# Revit family: Legrand Transformateur sec HP 2000kVA HN4AIAGPA
name_source: partatom
category: Equipement électrique
revit_build: Autodesk Revit 2018 (Build: 20170223_1515(x64)
units: mm (PartAtom-declared; Revit-internal decimal feet)

## family parameters
Basée sur le plan de construction = Non
Cote de connecteur circulaire = Utiliser le diamètre
Couper avec des vides une fois chargée = Non
Partagée = Non
Point de calcul de pièce = Non
Toujours verticalement = Oui
Type d'élément = Transformateur

## types (1)
- ZUHN4AIAGPA
    Classe d'isolement = 24 kV
    Conditions Générale d'Utilisation = https://export.legrand.com
    Coût = 0 $
    Description = Transformateur sec HP (Haute Performance) ZUHN4AIAGPA
    Enveloppe compatible IP31 = ZUBXS31CM
    Fabricant = Legrand
    Hauteur = 2420mm
    Ic - wheel centre line = 670
    Io = 0%
    Largeur = 2000mm
    LwA-Puissance acoustique = 71
    Pk at 120°C = 19000 W
    Po = 3100 W
    Poids = 6200Kg
    Puissance = 2000kVA
    R - wheel diameter = 160
    Tension = 20kV/410V
    Tension primaire = 20 kV
    Tension secondaire = 0 kV
    URL = www.legrand.fr
    Uk = 6%
    profondeur = 1310mm
    type = AAoAk
